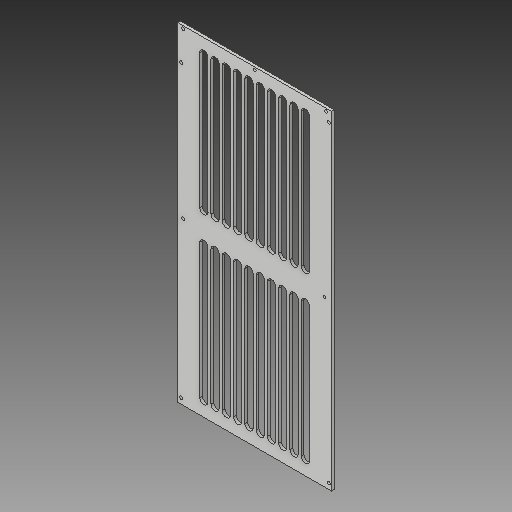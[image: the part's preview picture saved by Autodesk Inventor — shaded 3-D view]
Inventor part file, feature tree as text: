
AUTODESK INVENTOR PART (.ipt)
format: ipt  version: 2019 (Build 230136000, 136)  size: 272,384 bytes
history: native  units: in
note: dims shown in document units (in); Inventor stores cm internally (conversion verified against a paired STEP export)
features: sketch x4, extrude x3, hole x1
ambient origin geometry x8: Origin, YZ Plane, XZ Plane, XY Plane, X Axis, Y Axis, Z Axis, Center Point
bodies: Solid1 (feature_tree)
feature tree (8):
  extrude  "Extrusion1"  Depth=15.0in
  hole  "Hole1"  [1 undecoded]
  extrude  "Extrusion2"  Depth=1.5in
  extrude  "Extrusion3"  Depth=0.125in
  sketch  "Sketch1"  dims[d0=7.016in d1=15.0in]
  sketch  "Sketch2"  dims[d2=0.125in d3=0.0in d4=0.159in]
  sketch  "Sketch3"  dims[d5=0.25in d6=1.5in]
  sketch  "Sketch4"  dims[d7=90.0deg d8=0.125in d9=0.25in d10=0.125in d11=0.25in d12=0.14in d13=0.75in d14=0.375in d15=0.25in d16=0.5635in d17=1.0in d18=0.8108in d19=0.159in d21=0.125in d22=0.5in d23=0.125in d24=0.375in d34=0.5in d39=15.0in d40=6.0in d41=6.5in d44=3.937in d46=0.515in d47=0.3937in d49=1.0in d53=3.937in d55=0.515in d56=0.3937in d58=1.0in d60=1.0in d61=0.0in d63=6.5in d64=1.0in d65=1.0in d66=0.14in d68=0.14in d69=0.14in d70=0.0in d72=7.375in d74=3.258in d75=0.14in]
note: 1 required parameter value undecoded (feature->parameter linkage not recoverable at this tier; creation-order binding heuristic only, values carry confidence <= 0.55)
